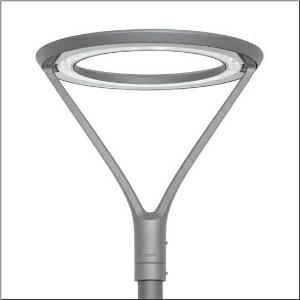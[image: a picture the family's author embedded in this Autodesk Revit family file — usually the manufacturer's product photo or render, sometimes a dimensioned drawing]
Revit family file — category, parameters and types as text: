
# Revit family: dl_20___pl1_2s_5xa512836s008_cd0e
name_source: partatom
category: Lighting Fixtures
units: mm (PartAtom-declared; Revit-internal decimal feet)

## family parameters
Cut with Voids When Loaded = No
Host = Face
Light Source = No
Part Type = Normal
Room Calculation Point = No
Round Connector Dimension = Use Diameter
Shared = No

## types (1)
- --- (1 x LED, 3050 lm, 28.6 W, 2700K)
    Apparent Load = 29 VA
    CIE Flux Codes = 33 78 99 100 100
    Color Rendering = 70
    Color Temperature = 2700K
    Default Elevation = 1800 mm
    Description = DL® 20, mast luminaire, primary light control with reflector, highly specular, primary optical cover: cover, of toughened safety glass of clear glass with excellent transmission level, light distribution: PL1.2s, light emission: direct distribution, primary light characteristic: symmetric, installation type: post-top, LED, High Power LED, rated luminous flux: 3.050lm, luminous efficacy: 107lm/W, light colour: 727, colour temperature: 2700K, control gear: Plus, control: flexible luminous flux parameterisation, time-dependent luminous flux control, constant luminous flux control, digital communication interface, power reduction, overheat protection, electronic power reduction, mains connection: 220..240V, 50/60Hz, connection cable pre-assembled, cable length: 5m, start of lifetime: 29W, end of service life: 29W, reduction: 15W, luminaire housing, upper part, of cast aluminium, powder-coated, Siteco® metallic grey (DB 702S), diameter: 690mm, height: 690mm, spigot size: 76mm (post-top), mounting height: 4..6m, luminaire housing, of cast aluminium, powder-coated, Siteco® metallic grey (DB 702S), equipment: standard, protection rating (complete): IP66, insulation class (complete): insulation class II (safety insulation), certification: CE, ENEC, VDE, impact resistance: IK08, permissible operating ambient temperature: -25..+35°C, standard-compliant lighting for roads and squares, packaging unit: 1 piece

Light Distribution: PL1.2s
    Height = 690 mm
    Lamp = 1 x LED
    Lamp Light Flux = 3050 lm
    Lamp Power = 28.6 W
    Lamp count = 1
    Length = 690 mm
    Luminous efficacy = 107 lm/W
    Manufacturer = Siteco
    ModVariant = No
    Model = 5XA512836S008
    Number of Poles = 1
    OnlyDefault = Yes
    Power Factor = 1
    Product Name = DL 20 | PL1.2s
    Product group = mast luminaire | pylon top
    ProductGroupID = 6100
    Protection Class = Protection class II
    Protection Degree = IP 66
    RLX_Detail_Level = 1
    RLX_Emergency_Light_Flux = 0 lm
    RLX_Emergency_Type = 0
    RLX_Emergency_Type_DB = No
    RlxData = <blob elided: 204445 chars, md5=ed6dc0dd>
    Socket = socket
    Standby Power = 0 W
    System Light Flux = 3050 lm
    System Power = 29 W
    Type Comments = factory setting: luminous flux: 100 % | dim-lin: 254 | 386 mA
    Type Image = l_1006001.jpg
    URL = http://relux.com
    VarID = @adj_084561
    Voltage = 0 V
    Weight = 0.00 kg
    Width = 0 mm  [stored 0 ft]

note: [stored X ft] marks values corroborated as IEEE doubles in the binary element streams (Revit-internal decimal feet)

## geometry (parser evidence)
native form markers: Blend x4, Sweep x10
no freeform markers — native parametric forms only
